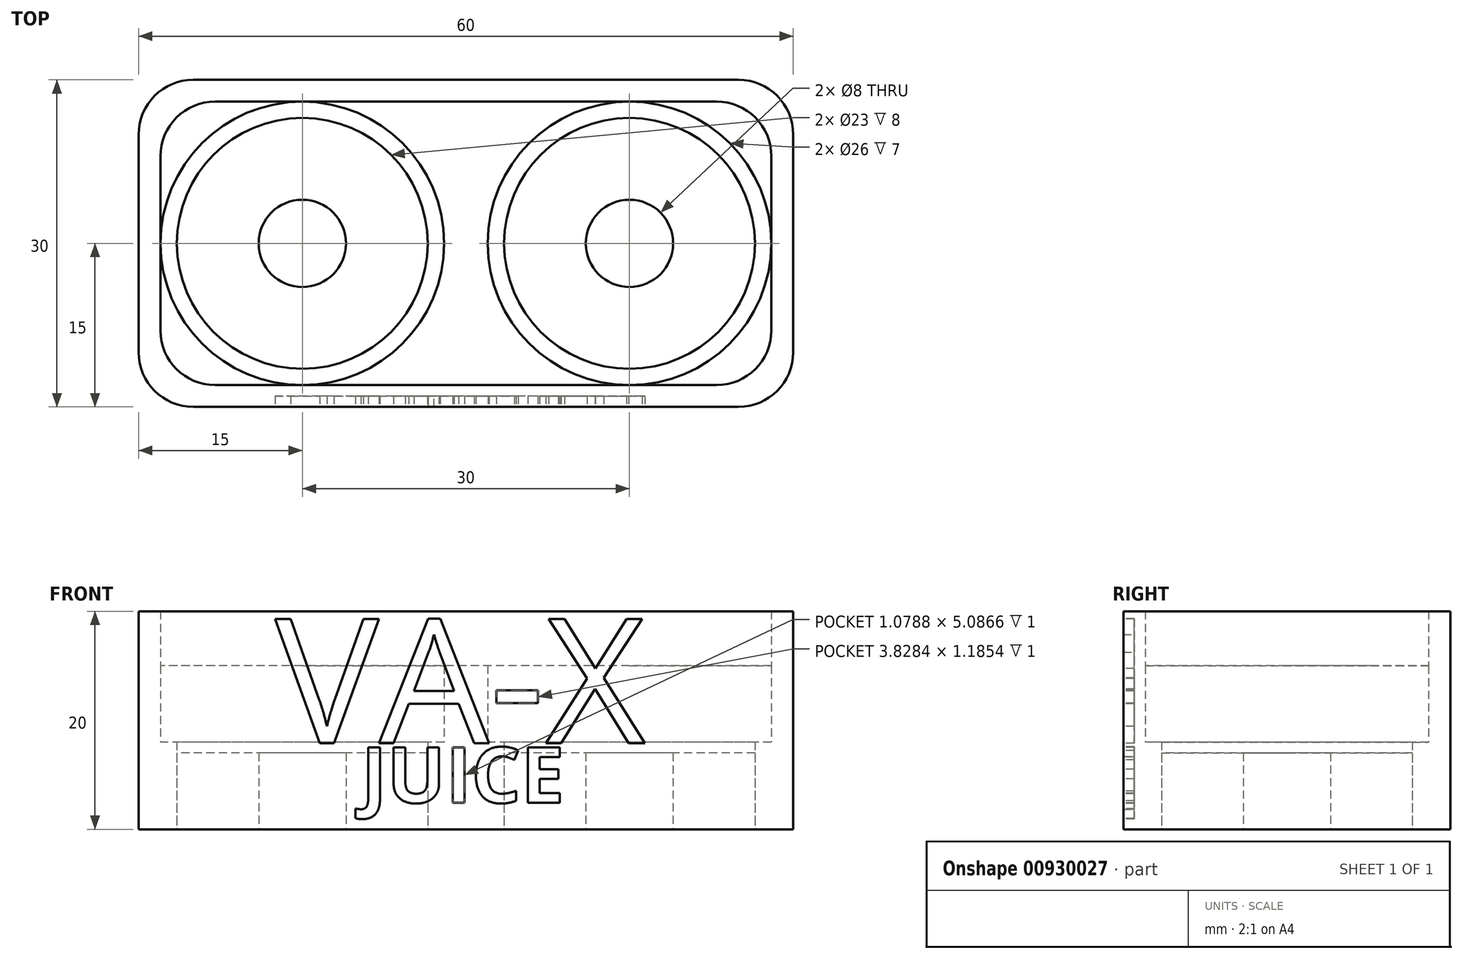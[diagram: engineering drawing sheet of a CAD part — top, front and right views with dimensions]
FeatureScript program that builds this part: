
annotation { "Feature Type Name" : "Feature", "Feature Type Description" : "" }
export const myFeature = defineFeature(function(context is Context, id is Id, definition is map)
    precondition{}
    {
        {
            var Q0;
            Q0=qCreatedBy(makeId("Top.planeOp"),FACE);
            var sketch = newSketch(context, id + "F0", { "sketchPlane" : qUnion([Q0])});
            skLineSegment(sketch, "E0.bottom", {"start": v(25, 15) * mm, "end": v(-25, 15) * mm});
            skLineSegment(sketch, "E0.top", {"start": v(25, -15) * mm, "end": v(-25, -15) * mm});
            skLineSegment(sketch, "E0.left", {"start": v(30, 10) * mm, "end": v(30, -10) * mm});
            skLineSegment(sketch, "E0.right", {"start": v(-30, 10) * mm, "end": v(-30, -10) * mm});
            skPoint(sketch, "E0.middle", {"position": v(0, 0) * mm});
            skLineSegment(sketch, "E1", {"start": v(-30, 0) * mm, "end": v(30, 0) * mm, "construction": true});
            skCircle(sketch, "E2", {"center": v(-15, 0) * mm, "radius": 13 * mm});
            skCircle(sketch, "E3", {"center": v(15, 0) * mm, "radius": 13 * mm});
            skCircle(sketch, "E4", {"center": v(-15, 0) * mm, "radius": 4 * mm});
            skCircle(sketch, "E5", {"center": v(15, 0) * mm, "radius": 4 * mm});
            skLineSegment(sketch, "E6.bottom", {"start": v(23, 13) * mm, "end": v(-23, 13) * mm});
            skLineSegment(sketch, "E6.top", {"start": v(23, -13) * mm, "end": v(-23, -13) * mm});
            skLineSegment(sketch, "E6.left", {"start": v(28, 8) * mm, "end": v(28, -8) * mm});
            skLineSegment(sketch, "E6.right", {"start": v(-28, 8) * mm, "end": v(-28, -8) * mm});
            skCircle(sketch, "E7", {"center": v(15, 0) * mm, "radius": 11.5 * mm});
            skCircle(sketch, "E8", {"center": v(-15, 0) * mm, "radius": 11.5 * mm});
            skPoint(sketch, "E9.visualSharp", {"position": v(-30, 15) * mm});
            skArc(sketch, "E9.filletArc", {"start": v(-25, 15) * mm, "mid": v(-28.54, 13.54) * mm, "end": v(-30, 10) * mm});
            skPoint(sketch, "E10.visualSharp", {"position": v(-28, 13) * mm});
            skArc(sketch, "E10.filletArc", {"start": v(-23, 13) * mm, "mid": v(-26.54, 11.54) * mm, "end": v(-28, 8) * mm});
            skPoint(sketch, "E11.visualSharp", {"position": v(28, 13) * mm});
            skArc(sketch, "E11.filletArc", {"start": v(28, 8) * mm, "mid": v(26.54, 11.54) * mm, "end": v(23, 13) * mm});
            skPoint(sketch, "E12.visualSharp", {"position": v(30, 15) * mm});
            skArc(sketch, "E12.filletArc", {"start": v(30, 10) * mm, "mid": v(28.54, 13.54) * mm, "end": v(25, 15) * mm});
            skPoint(sketch, "E13.visualSharp", {"position": v(28, -13) * mm});
            skArc(sketch, "E13.filletArc", {"start": v(23, -13) * mm, "mid": v(26.54, -11.54) * mm, "end": v(28, -8) * mm});
            skPoint(sketch, "E14.visualSharp", {"position": v(30, -15) * mm});
            skArc(sketch, "E14.filletArc", {"start": v(25, -15) * mm, "mid": v(28.54, -13.54) * mm, "end": v(30, -10) * mm});
            skPoint(sketch, "E15.visualSharp", {"position": v(-28, -13) * mm});
            skArc(sketch, "E15.filletArc", {"start": v(-28, -8) * mm, "mid": v(-26.54, -11.54) * mm, "end": v(-23, -13) * mm});
            skPoint(sketch, "E16.visualSharp", {"position": v(-30, -15) * mm});
            skArc(sketch, "E16.filletArc", {"start": v(-30, -10) * mm, "mid": v(-28.54, -13.54) * mm, "end": v(-25, -15) * mm});
            skSolve(sketch);
        }
        {
            var Q0;
            Q0=makeQuery(id+"F0.imprint","IMPRINT",FACE,{"disambiguationData":[TD([[makeQuery(id+"F0.imprint","IMPRINT",EDGE,{"derivedFrom":sQuery(id+"F0.wireOp",EDGE,"E2")}),1.0]])]});
            var Q1;
            Q1=makeQuery(id+"F0.imprint","IMPRINT",FACE,{"disambiguationData":[TD([[makeQuery(id+"F0.imprint","IMPRINT",EDGE,{"derivedFrom":sQuery(id+"F0.wireOp",EDGE,"E3")}),1.0]])]});
            extrude(context, id + "F1", {"entities" : qUnion([Q0, Q1]), "depth" : 8 * mm, "offsetDistance" : 25 * mm});
        }
        {
            var Q0;
            Q0=makeQuery(id+"F0.imprint","IMPRINT",FACE,{"disambiguationData":[TD([[makeQuery(id+"F0.imprint","IMPRINT",EDGE,{"derivedFrom":sQuery(id+"F0.wireOp",EDGE,"E2")}),-1.0]])]});
            var Q1;
            {var subQ5=sQuery(id+"F0.wireOp",EDGE,"E11.filletArc");Q1=makeQuery(id+"F0.imprint","IMPRINT",FACE,{"disambiguationData":[TD([[makeQuery(id+"F0.imprint","IMPRINT",EDGE,{"derivedFrom":subQ5}),1.0]])]});}
            var Q2;
            {var subQ5=sQuery(id+"F0.wireOp",EDGE,"E13.filletArc");Q2=makeQuery(id+"F0.imprint","IMPRINT",FACE,{"disambiguationData":[TD([[makeQuery(id+"F0.imprint","IMPRINT",EDGE,{"derivedFrom":subQ5}),1.0]])]});}
            extrude(context, id + "F2", {"entities" : qUnion([Q0, Q1, Q2]), "depth" : 15 * mm, "offsetDistance" : 25 * mm});
        }
        {
            var Q0;
            Q0=makeQuery(id+"F0.imprint","IMPRINT",FACE,{"disambiguationData":[TD([[makeQuery(id+"F0.imprint","IMPRINT",EDGE,{"derivedFrom":sQuery(id+"F0.wireOp",EDGE,"E0.bottom")}),1.0]])]});
            extrude(context, id + "F3", {"entities" : qUnion([Q0]), "operationType" : NewBodyOperationType.ADD, "depth" : 20 * mm, "offsetDistance" : 25 * mm});
        }
        {
            var Q0;
            Q0=makeQuery(id+"F0.imprint","IMPRINT",FACE,{"disambiguationData":[TD([[makeQuery(id+"F0.imprint","IMPRINT",EDGE,{"derivedFrom":sQuery(id+"F0.wireOp",EDGE,"E4")}),-1.0]])]});
            var Q1;
            Q1=makeQuery(id+"F0.imprint","IMPRINT",FACE,{"disambiguationData":[TD([[makeQuery(id+"F0.imprint","IMPRINT",EDGE,{"derivedFrom":sQuery(id+"F0.wireOp",EDGE,"E5")}),-1.0]])]});
            extrude(context, id + "F4", {"entities" : qUnion([Q0, Q1]), "depth" : 7 * mm, "offsetDistance" : 25 * mm});
        }
        {
            var Q0;
            Q0=makeQuery(id+"F3.opExtrude","SWEPT_FACE",FACE,{"disambiguationData":[OSD([sQuery(id+"F0.wireOp",EDGE,"E0.top")])]});
            var sketch = newSketch(context, id + "F5", { "sketchPlane" : qUnion([Q0])});
            skLineSegment(sketch, "E17.bottom", {"start": v(-25, 20) * mm, "end": v(25, 20) * mm});
            skLineSegment(sketch, "E17.top", {"start": v(-25, 0) * mm, "end": v(25, 0) * mm});
            skLineSegment(sketch, "E17.left", {"start": v(-25, 20) * mm, "end": v(-25, 0) * mm});
            skLineSegment(sketch, "E17.right", {"start": v(25, 20) * mm, "end": v(25, 0) * mm});
            skText(sketch, "E18", { "text": "VA-X", "fontName": "OpenSans-Regular.ttf"});
            skLineSegment(sketch, "E19", {"start": v(0, 0) * mm, "end": v(0, 20) * mm, "construction": true});
            skText(sketch, "E20", { "text": "JUICE", "fontName": "OpenSans-Bold.ttf"});
            const initialGuessF5  = {"E18": [-0.01748, 0.00788, 1, 0, 0.0115], "E20": [-0.0096, 0.00243, 1, 0, 0.00513]};
            skSetInitialGuess(sketch, initialGuessF5);
            skSolve(sketch);
        }
        {
            var Q0;
            Q0=makeQuery(id+"F5.imprint","IMPRINT",FACE,{"disambiguationData":[TD([[makeQuery(id+"F5.imprint","IMPRINT",EDGE,{"derivedFrom":sQuery(id+"F5.wireOp",EDGE,"E18.sketch_text.stroke-0")}),-1.0]])]});
            var Q1;
            Q1=makeQuery(id+"F5.imprint","IMPRINT",FACE,{"disambiguationData":[TD([[makeQuery(id+"F5.imprint","IMPRINT",EDGE,{"derivedFrom":sQuery(id+"F5.wireOp",EDGE,"E18.sketch_text.stroke-9")}),-1.0]])]});
            var Q2;
            Q2=makeQuery(id+"F5.imprint","IMPRINT",FACE,{"disambiguationData":[TD([[makeQuery(id+"F5.imprint","IMPRINT",EDGE,{"derivedFrom":sQuery(id+"F5.wireOp",EDGE,"E18.sketch_text.stroke-22")}),-1.0]])]});
            var Q3;
            Q3=makeQuery(id+"F5.imprint","IMPRINT",FACE,{"disambiguationData":[TD([[makeQuery(id+"F5.imprint","IMPRINT",EDGE,{"derivedFrom":sQuery(id+"F5.wireOp",EDGE,"E18.sketch_text.stroke-26")}),-1.0]])]});
            var Q4;
            Q4=makeQuery(id+"F5.imprint","IMPRINT",FACE,{"disambiguationData":[TD([[makeQuery(id+"F5.imprint","IMPRINT",EDGE,{"derivedFrom":sQuery(id+"F5.wireOp",EDGE,"E20.sketch_text.stroke-0")}),-1.0]])]});
            var Q5;
            Q5=makeQuery(id+"F5.imprint","IMPRINT",FACE,{"disambiguationData":[TD([[makeQuery(id+"F5.imprint","IMPRINT",EDGE,{"derivedFrom":sQuery(id+"F5.wireOp",EDGE,"E20.sketch_text.stroke-10")}),-1.0]])]});
            var Q6;
            Q6=makeQuery(id+"F5.imprint","IMPRINT",FACE,{"disambiguationData":[TD([[makeQuery(id+"F5.imprint","IMPRINT",EDGE,{"derivedFrom":sQuery(id+"F5.wireOp",EDGE,"E20.sketch_text.stroke-25")}),-1.0]])]});
            var Q7;
            Q7=makeQuery(id+"F5.imprint","IMPRINT",FACE,{"disambiguationData":[TD([[makeQuery(id+"F5.imprint","IMPRINT",EDGE,{"derivedFrom":sQuery(id+"F5.wireOp",EDGE,"E20.sketch_text.stroke-29")}),-1.0]])]});
            var Q8;
            Q8=makeQuery(id+"F5.imprint","IMPRINT",FACE,{"disambiguationData":[TD([[makeQuery(id+"F5.imprint","IMPRINT",EDGE,{"derivedFrom":sQuery(id+"F5.wireOp",EDGE,"E20.sketch_text.stroke-44")}),-1.0]])]});
            extrude(context, id + "F6", {"entities" : qUnion([Q0, Q1, Q2, Q3, Q4, Q5, Q6, Q7, Q8]), "operationType" : NewBodyOperationType.REMOVE, "oppositeDirection" : true, "depth" : 1 * mm, "offsetDistance" : 25 * mm});
        }
    });
